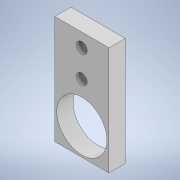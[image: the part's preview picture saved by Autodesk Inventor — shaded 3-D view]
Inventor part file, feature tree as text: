
AUTODESK INVENTOR PART (.ipt)
format: ipt  version: 2022.1 (Build 261234000, 234)  size: 115,200 bytes
history: native  units: in
note: dims shown in document units (in); Inventor stores cm internally (conversion verified against a paired STEP export)
features: extrude x1, sketch x1
ambient origin geometry x8: Origin, YZ Plane, XZ Plane, XY Plane, X Axis, Y Axis, Z Axis, Center Point
bodies: Solid1 (feature_tree)
feature tree (2):
  extrude  "Extrusion1"  Depth=2.0in
  sketch  "Sketch1"  dims[d0=1.0in d1=2.0in d2=0.1969in d3=0.1969in d4=0.5in d5=0.25in d6=0.75in d7=0.925in d8=0.3in d9=0.0in]
